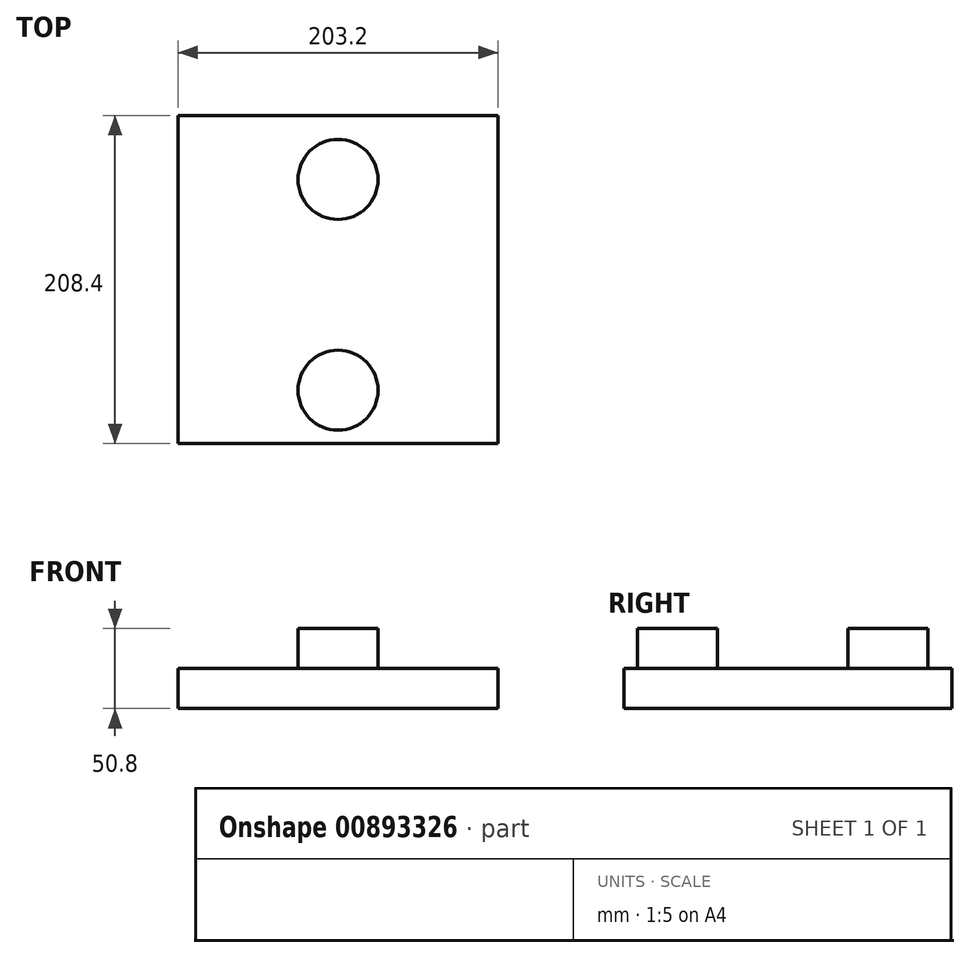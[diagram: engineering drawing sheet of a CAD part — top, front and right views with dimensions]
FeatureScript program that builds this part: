
annotation { "Feature Type Name" : "Feature", "Feature Type Description" : "" }
export const myFeature = defineFeature(function(context is Context, id is Id, definition is map)
    precondition{}
    {
        {
            var Q0;
            Q0=qCreatedBy(makeId("Top.planeOp"),FACE);
            var sketch = newSketch(context, id + "F0", { "sketchPlane" : qUnion([Q0])});
            skLineSegment(sketch, "E0.bottom", {"start": v(-101.6, 104.2) * mm, "end": v(101.6, 104.2) * mm});
            skLineSegment(sketch, "E0.top", {"start": v(-101.6, -104.2) * mm, "end": v(101.6, -104.2) * mm});
            skLineSegment(sketch, "E0.left", {"start": v(-101.6, 104.2) * mm, "end": v(-101.6, -104.2) * mm});
            skLineSegment(sketch, "E0.right", {"start": v(101.6, 104.2) * mm, "end": v(101.6, -104.2) * mm});
            skSolve(sketch);
        }
        {
            var Q0;
            Q0=qSketchRegion(id+"F0",true);
            extrude(context, id + "F1", {"entities" : qUnion([Q0]), "depth" : 25.4 * mm, "offsetDistance" : 25.4 * mm});
        }
        {
            var Q0;
            Q0=makeQuery(id+"F1.opExtrude","CAP_FACE",FACE,{"disambiguationData":[OSD([sQuery(id+"F0.wireOp",EDGE,"E0.bottom"),sQuery(id+"F0.wireOp",EDGE,"E0.top"),sQuery(id+"F0.wireOp",EDGE,"E0.left"),sQuery(id+"F0.wireOp",EDGE,"E0.right")])],"isStart":false});
            var sketch = newSketch(context, id + "F2", { "sketchPlane" : qUnion([Q0])});
            skCircle(sketch, "E1", {"center": v(0, 63.5) * mm, "radius": 25.4 * mm});
            skSolve(sketch);
        }
        {
            var Q0;
            Q0=qSketchRegion(id+"F2",true);
            extrude(context, id + "F3", {"entities" : qUnion([Q0]), "operationType" : NewBodyOperationType.ADD, "depth" : 25.4 * mm, "offsetDistance" : 25.4 * mm});
        }
        {
            var Q0;
            Q0=makeQuery(id+"F1.opExtrude","CAP_FACE",FACE,{"disambiguationData":[OSD([sQuery(id+"F0.wireOp",EDGE,"E0.bottom"),sQuery(id+"F0.wireOp",EDGE,"E0.top"),sQuery(id+"F0.wireOp",EDGE,"E0.left"),sQuery(id+"F0.wireOp",EDGE,"E0.right")])],"isStart":false});
            var sketch = newSketch(context, id + "F4", { "sketchPlane" : qUnion([Q0])});
            skCircle(sketch, "E2", {"center": v(0, -70.36) * mm, "radius": 25.4 * mm});
            skSolve(sketch);
        }
        {
            var Q0;
            Q0=qSketchRegion(id+"F4",true);
            var Q1;
            Q1=makeQuery(id+"F3.opExtrude","CAP_FACE",FACE,{"disambiguationData":[OSD([sQuery(id+"F2.wireOp",EDGE,"E1")])],"isStart":false});
            extrude(context, id + "F5", {"entities" : qUnion([Q0]), "operationType" : NewBodyOperationType.ADD, "endBound" : BoundingType.UP_TO_SURFACE, "depth" : 25.4 * mm, "endBoundEntityFace" : qUnion([Q1]), "offsetDistance" : 25.4 * mm});
        }
    });
